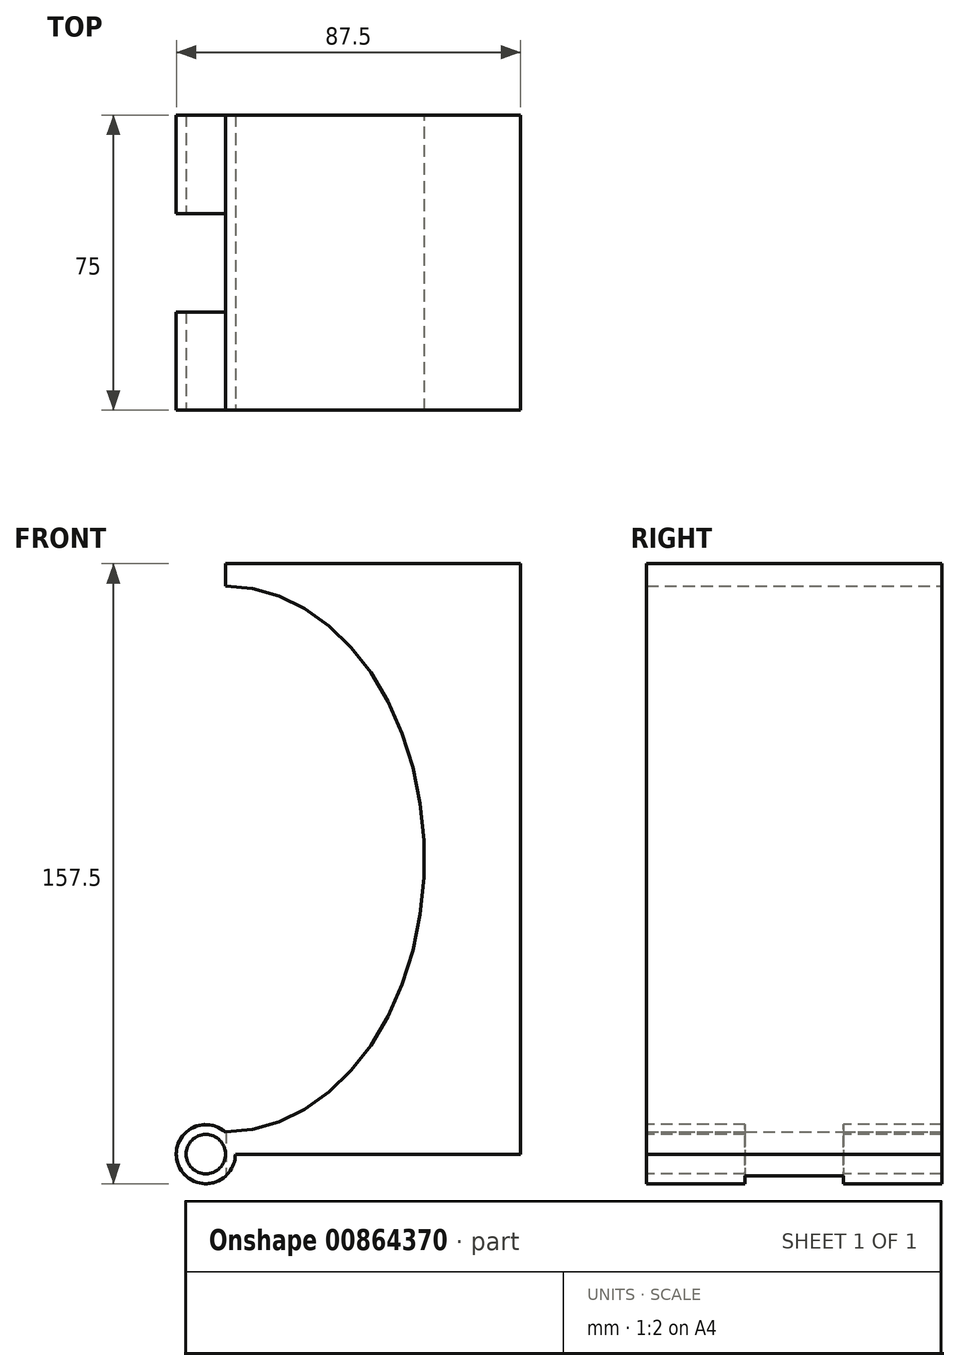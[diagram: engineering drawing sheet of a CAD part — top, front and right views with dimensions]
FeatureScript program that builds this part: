
annotation { "Feature Type Name" : "Feature", "Feature Type Description" : "" }
export const myFeature = defineFeature(function(context is Context, id is Id, definition is map)
    precondition{}
    {
        {
            var Q0;
            Q0=qCreatedBy(makeId("Front.planeOp"),FACE);
            var sketch = newSketch(context, id + "F0", { "sketchPlane" : qUnion([Q0])});
            skLineSegment(sketch, "E0.bottom", {"start": v(169.52, -36.28) * mm, "end": v(19.52, -36.28) * mm});
            skLineSegment(sketch, "E0.top", {"start": v(169.52, 113.72) * mm, "end": v(19.52, 113.72) * mm});
            skLineSegment(sketch, "E0.left", {"start": v(169.52, -36.28) * mm, "end": v(169.52, 113.72) * mm});
            skLineSegment(sketch, "E0.right", {"start": v(19.52, -36.28) * mm, "end": v(19.52, 113.72) * mm});
            skPoint(sketch, "E0.middle", {"position": v(94.52, 38.72) * mm});
            skEllipse(sketch, "E1", {"center": v(94.52, 38.72) * mm, "majorRadius": 69.33 * mm, "minorRadius": 50.52 * mm, "majorAxis": v(0, -1)});
            skLineSegment(sketch, "E2", {"start": v(94.52, 113.72) * mm, "end": v(94.52, -36.28) * mm});
            skSolve(sketch);
        }
        {
            var Q0;
            {var subQ4=sQuery(id+"F0.wireOp",EDGE,"E0.left");Q0=makeQuery(id+"F0.imprint","IMPRINT",FACE,{"disambiguationData":[TD([[makeQuery(id+"F0.imprint","IMPRINT",EDGE,{"derivedFrom":subQ4}),1.0]])]});}
            extrude(context, id + "F1", {"entities" : qUnion([Q0]), "depth" : 75 * mm, "offsetDistance" : 25 * mm});
        }
        {
            var Q0;
            Q0=makeQuery(id+"F1.opExtrude","CAP_FACE",FACE,{"disambiguationData":[OSD([sQuery(id+"F0.wireOp",EDGE,"E0.bottom"),sQuery(id+"F0.wireOp",EDGE,"E0.top"),sQuery(id+"F0.wireOp",EDGE,"E0.left"),sQuery(id+"F0.wireOp",EDGE,"E1"),sQuery(id+"F0.wireOp",EDGE,"E2")])],"isStart":false});
            var sketch = newSketch(context, id + "F2", { "sketchPlane" : qUnion([Q0])});
            skCircle(sketch, "E3", {"center": v(89.52, -36.28) * mm, "radius": 7.5 * mm});
            skSolve(sketch);
        }
        {
            var Q0;
            {var subQ0=sQuery(id+"F2.wireOp",EDGE,"E3");var subQ1=sQuery(id+"F0.wireOp",EDGE,"E0.bottom");var subQ2=makeQuery(id+"F1.opExtrude","CAP_EDGE",EDGE,{"disambiguationData":[OSD([subQ1])],"isStart":false});var subQ3=makeQuery(id+"F2.imprint","INTERSECT",VERTEX,{"derivedFrom":[subQ2,subQ0]});Q0=makeQuery(id+"F2.imprint","IMPRINT",FACE,{"disambiguationData":[TD([[makeQuery(id+"F2.imprint","IMPRINT",EDGE,{"disambiguationData":[TD([[subQ3,1.0]])],"derivedFrom":subQ0}),1.0]])]});}
            extrude(context, id + "F3", {"entities" : qUnion([Q0]), "operationType" : NewBodyOperationType.ADD, "oppositeDirection" : true, "depth" : 75 * mm, "offsetDistance" : 25 * mm});
        }
        {
            var Q0;
            {var subQ0=sQuery(id+"F0.wireOp",EDGE,"E2");var subQ1=sQuery(id+"F0.wireOp",EDGE,"E0.bottom");Q0=makeQuery(id+"F3.boolean.opBoolean","MERGE",FACE,{"derivedFrom":[makeQuery(id+"F1.opExtrude","CAP_FACE",FACE,{"disambiguationData":[OSD([subQ1,sQuery(id+"F0.wireOp",EDGE,"E0.top"),sQuery(id+"F0.wireOp",EDGE,"E0.left"),sQuery(id+"F0.wireOp",EDGE,"E1"),subQ0])],"isStart":false}),makeQuery(id+"F3.opExtrude","CAP_FACE",FACE,{"disambiguationData":[OSD([subQ1,subQ0,sQuery(id+"F2.wireOp",EDGE,"E3")])],"isStart":true})]});}
            var sketch = newSketch(context, id + "F4", { "sketchPlane" : qUnion([Q0])});
            skCircle(sketch, "E4", {"center": v(89.52, -36.28) * mm, "radius": 5 * mm});
            skSolve(sketch);
        }
        {
            var Q0;
            Q0=makeQuery(id+"F4.imprint","IMPRINT",FACE,{"disambiguationData":[TD([[makeQuery(id+"F4.imprint","IMPRINT",EDGE,{"derivedFrom":sQuery(id+"F4.wireOp",EDGE,"E4")}),1.0]])]});
            extrude(context, id + "F5", {"entities" : qUnion([Q0]), "operationType" : NewBodyOperationType.REMOVE, "oppositeDirection" : true, "depth" : 75 * mm, "offsetDistance" : 25 * mm});
        }
        {
            var Q0;
            Q0=qCreatedBy(makeId("Right.planeOp"),FACE);
            var sketch = newSketch(context, id + "F6", { "sketchPlane" : qUnion([Q0])});
            skLineSegment(sketch, "E5.bottom", {"start": v(-25, -16.22) * mm, "end": v(-50, -16.22) * mm});
            skLineSegment(sketch, "E5.top", {"start": v(-25, -66.22) * mm, "end": v(-50, -66.22) * mm});
            skLineSegment(sketch, "E5.left", {"start": v(-25, -16.22) * mm, "end": v(-25, -66.22) * mm});
            skLineSegment(sketch, "E5.right", {"start": v(-50, -16.22) * mm, "end": v(-50, -66.22) * mm});
            skSolve(sketch);
        }
        {
            var Q0;
            Q0=makeQuery(id+"F6.imprint","IMPRINT",FACE,{"disambiguationData":[TD([[makeQuery(id+"F6.imprint","IMPRINT",EDGE,{"derivedFrom":sQuery(id+"F6.wireOp",EDGE,"E5.bottom")}),1.0]])]});
            extrude(context, id + "F7", {"entities" : qUnion([Q0]), "operationType" : NewBodyOperationType.REMOVE, "depth" : 94.6 * mm, "offsetDistance" : 25 * mm});
        }
    });
